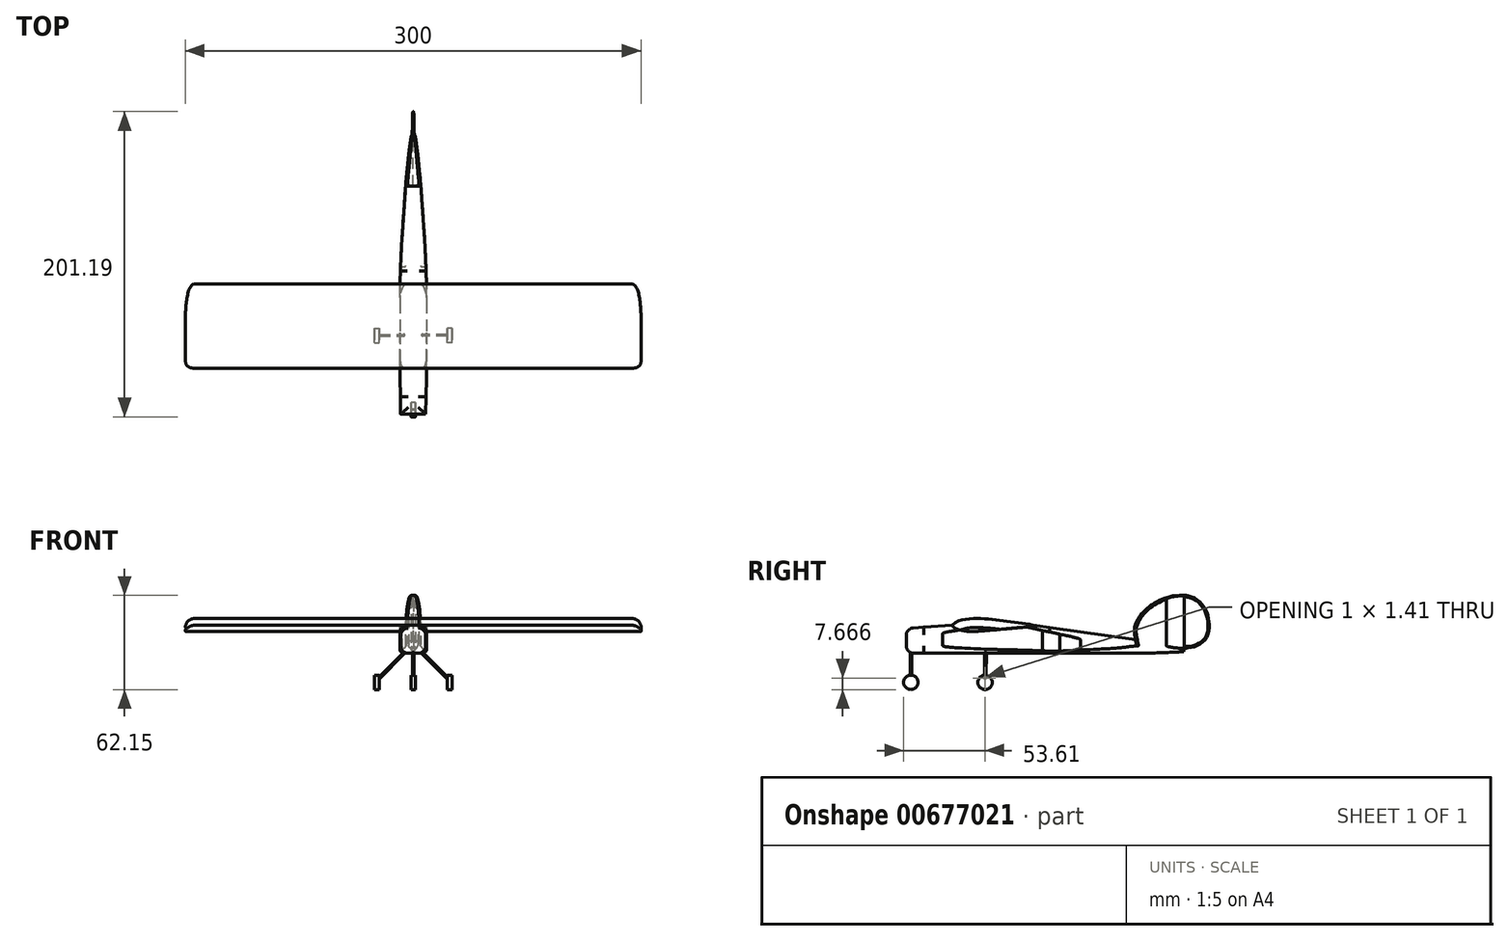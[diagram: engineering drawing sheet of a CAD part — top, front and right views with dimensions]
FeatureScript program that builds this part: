
annotation { "Feature Type Name" : "Feature", "Feature Type Description" : "" }
export const myFeature = defineFeature(function(context is Context, id is Id, definition is map)
    precondition{}
    {
        {
            var Q0;
            Q0=qCreatedBy(makeId("Top.planeOp"),FACE);
            var sketch = newSketch(context, id + "F0", { "sketchPlane" : qUnion([Q0])});
            skPoint(sketch, "E0", {"position": v(-29, 19.94) * mm});
            skLineSegment(sketch, "E1", {"start": v(0, 0) * mm, "end": v(8.25, 0) * mm});
            skLineSegment(sketch, "E2", {"start": v(8.25, 0) * mm, "end": v(8.4, 11.66) * mm});
            skLineSegment(sketch, "E3", {"start": v(8.4, 11.66) * mm, "end": v(8.64, 23.9) * mm});
            skLineSegment(sketch, "E4", {"start": v(8.64, 23.9) * mm, "end": v(8.64, 30.7) * mm});
            skLineSegment(sketch, "E5", {"start": v(8.64, 30.7) * mm, "end": v(8.64, 38.91) * mm});
            skLineSegment(sketch, "E6", {"start": v(8.64, 38.91) * mm, "end": v(8.64, 53.75) * mm});
            skLineSegment(sketch, "E7", {"start": v(8.64, 53.75) * mm, "end": v(8.71, 73.84) * mm});
            skLineSegment(sketch, "E8", {"start": v(8.71, 73.84) * mm, "end": v(8.71, 77.09) * mm});
            skLineSegment(sketch, "E9", {"start": v(8.71, 77.09) * mm, "end": v(8.61, 89.68) * mm});
            skLineSegment(sketch, "E10", {"start": v(8.61, 89.68) * mm, "end": v(8.2, 101.14) * mm});
            skLineSegment(sketch, "E11", {"start": v(8.2, 101.14) * mm, "end": v(7.51, 114.78) * mm});
            skLineSegment(sketch, "E12", {"start": v(7.51, 114.78) * mm, "end": v(5.18, 148.4) * mm});
            skLineSegment(sketch, "E13", {"start": v(5.18, 148.4) * mm, "end": v(3.01, 171.13) * mm});
            skLineSegment(sketch, "E14", {"start": v(3.01, 171.13) * mm, "end": v(1.43, 183.1) * mm});
            skLineSegment(sketch, "E15", {"start": v(1.43, 183.1) * mm, "end": v(0.72, 183.1) * mm});
            skLineSegment(sketch, "E16", {"start": v(0, 0) * mm, "end": v(0, 183.1) * mm});
            skLineSegment(sketch, "E17.MirrorCS", {"start": v(-5.18, 148.4) * mm, "end": v(-3.01, 171.13) * mm});
            skLineSegment(sketch, "E18.MirrorCS", {"start": v(-3.01, 171.13) * mm, "end": v(-1.43, 183.1) * mm});
            skLineSegment(sketch, "E19.MirrorCS", {"start": v(-1.43, 183.1) * mm, "end": v(-0.72, 183.1) * mm});
            skLineSegment(sketch, "E20.MirrorCS", {"start": v(-7.51, 114.78) * mm, "end": v(-5.18, 148.4) * mm});
            skLineSegment(sketch, "E21.MirrorCS", {"start": v(-8.61, 89.68) * mm, "end": v(-8.2, 101.14) * mm});
            skLineSegment(sketch, "E22.MirrorCS", {"start": v(-8.71, 77.09) * mm, "end": v(-8.61, 89.68) * mm});
            skLineSegment(sketch, "E23.MirrorCS", {"start": v(-8.2, 101.14) * mm, "end": v(-7.51, 114.78) * mm});
            skLineSegment(sketch, "E24.MirrorCS", {"start": v(-8.64, 53.75) * mm, "end": v(-8.71, 73.84) * mm});
            skLineSegment(sketch, "E25.MirrorCS", {"start": v(-8.64, 38.91) * mm, "end": v(-8.64, 53.75) * mm});
            skLineSegment(sketch, "E26.MirrorCS", {"start": v(-8.64, 23.9) * mm, "end": v(-8.64, 30.7) * mm});
            skLineSegment(sketch, "E27.MirrorCS", {"start": v(-8.64, 30.7) * mm, "end": v(-8.64, 38.91) * mm});
            skLineSegment(sketch, "E28.MirrorCS", {"start": v(-8.4, 11.66) * mm, "end": v(-8.64, 23.9) * mm});
            skLineSegment(sketch, "E29.MirrorCS", {"start": v(-8.25, 0) * mm, "end": v(-8.4, 11.66) * mm});
            skLineSegment(sketch, "E30", {"start": v(-0.72, 183.1) * mm, "end": v(-0.34, 199.72) * mm});
            skLineSegment(sketch, "E31", {"start": v(0.72, 183.1) * mm, "end": v(0.31, 199.7) * mm});
            skArc(sketch, "E32", {"start": v(0.31, 199.7) * mm, "mid": v(0, 200.02) * mm, "end": v(-0.34, 199.72) * mm});
            skLineSegment(sketch, "E33", {"start": v(-8.25, 0) * mm, "end": v(0, 0) * mm});
            skLineSegment(sketch, "E34", {"start": v(-8.71, 73.84) * mm, "end": v(-8.71, 77.09) * mm});
            skSolve(sketch);
        }
        {
            var Q0;
            Q0=qCreatedBy(makeId("Right.planeOp"),FACE);
            var sketch = newSketch(context, id + "F1", { "sketchPlane" : qUnion([Q0])});
            skPoint(sketch, "E35", {"position": v(9.53, 28.77) * mm});
            skLineSegment(sketch, "E36", {"start": v(9.53, 28.77) * mm, "end": v(9.53, 58.18) * mm});
            skLineSegment(sketch, "E37", {"start": v(0, 6.73) * mm, "end": v(0, 7.52) * mm});
            skLineSegment(sketch, "E38", {"start": v(0, 7.52) * mm, "end": v(30.35, 9.6) * mm});
            skFitSpline(sketch, "E39", {"points": [v(30.35, 9.6) * mm, v(30.74, 8.85) * mm, v(32.06, 7.7) * mm, v(33.67, 6.97) * mm, v(36.02, 6.27) * mm, v(40.27, 5.57) * mm, v(46.3, 5.57) * mm, v(51.85, 6) * mm, v(61.06, 6.76) * mm, v(70.26, 7.62) * mm, v(83.75, 8.9) * mm, v(85.82, 9.15) * mm], "startDerivative": vector(7.09, -18.14) * mm, "endDerivative": vector(24.4, 3.5) * mm});
            skLineSegment(sketch, "E40", {"start": v(85.82, 9.15) * mm, "end": v(94.4, 8) * mm});
            skLineSegment(sketch, "E41", {"start": v(94.4, 8) * mm, "end": v(130.2, 2.9) * mm});
            skLineSegment(sketch, "E42", {"start": v(130.2, 2.9) * mm, "end": v(150.98, -0.06) * mm});
            skLineSegment(sketch, "E43", {"start": v(150.98, -0.06) * mm, "end": v(150.98, -0.8) * mm});
            skLineSegment(sketch, "E44", {"start": v(150.98, -0.8) * mm, "end": v(182.74, -5.52) * mm});
            skLineSegment(sketch, "E45", {"start": v(182.74, -5.52) * mm, "end": v(182.74, -8.83) * mm});
            skLineSegment(sketch, "E46", {"start": v(182.74, -8.83) * mm, "end": v(97.77, -8.9) * mm});
            skLineSegment(sketch, "E47", {"start": v(97.77, -8.9) * mm, "end": v(15.77, -8.9) * mm});
            skLineSegment(sketch, "E48", {"start": v(15.77, -8.9) * mm, "end": v(0, -8.9) * mm});
            skLineSegment(sketch, "E49", {"start": v(0, -8.9) * mm, "end": v(0, 0) * mm});
            skFitSpline(sketch, "E50", {"points": [v(30.35, 9.6) * mm, v(31.65, 10.88) * mm, v(34.45, 12.35) * mm, v(39.4, 13.6) * mm, v(44.05, 13.96) * mm, v(51.46, 13.89) * mm, v(60.53, 13.02) * mm, v(70.8, 11.66) * mm, v(80.77, 10.16) * mm, v(85.82, 9.15) * mm], "startDerivative": vector(18.65, 21.26) * mm, "endDerivative": vector(44.49, -9.56) * mm});
            skFitSpline(sketch, "E51", {"points": [v(150.98, -0.06) * mm, v(150.73, 1.38) * mm, v(150.26, 4.22) * mm, v(150.22, 7.02) * mm, v(151.56, 11.72) * mm, v(154.77, 16.71) * mm, v(161.1, 22.75) * mm, v(167.85, 26.44) * mm, v(173.09, 28.4) * mm, v(178.35, 29.11) * mm, v(183.08, 29.3) * mm, v(188.07, 28.35) * mm, v(192.81, 25.62) * mm, v(197.13, 20.08) * mm, v(198.92, 15.11) * mm, v(199.6, 10.29) * mm, v(199.64, 7.48) * mm, v(199.22, 4.9) * mm, v(197.73, 0.97) * mm, v(194.97, -1.94) * mm, v(190.97, -4.24) * mm, v(186.66, -5.33) * mm, v(182.74, -5.52) * mm], "startDerivative": vector(-8.61, 50.6) * mm, "endDerivative": vector(-92.07, -0.95) * mm});
            skLineSegment(sketch, "E52", {"start": v(0, 6.73) * mm, "end": v(0, 0) * mm});
            skSolve(sketch);
        }
        {
            var Q0;
            Q0 = qSketchRegion(id + "F1", true);
            extrude(context, id + "F2", {"entities" : qUnion([Q0]), "endBound" : BoundingType.SYMMETRIC, "depth" : 100 * mm, "offsetDistance" : 25 * mm});
        }
        {
            var Q0;
            Q0 = qSketchRegion(id + "F0", true);
            extrude(context, id + "F3", {"entities" : qUnion([Q0]), "endBound" : BoundingType.SYMMETRIC, "depth" : 100 * mm, "offsetDistance" : 25 * mm});
        }
        {
            var Q0;
            Q0=makeQuery(id+"F2.opExtrude","SWEPT_BODY",BODY,{"disambiguationData":[OSD([sQuery(id+"F1.wireOp",EDGE,"E37"),sQuery(id+"F1.wireOp",EDGE,"E38"),sQuery(id+"F1.wireOp",EDGE,"E40"),sQuery(id+"F1.wireOp",EDGE,"E41"),sQuery(id+"F1.wireOp",EDGE,"E42"),sQuery(id+"F1.wireOp",EDGE,"E45"),sQuery(id+"F1.wireOp",EDGE,"E46"),sQuery(id+"F1.wireOp",EDGE,"E47"),sQuery(id+"F1.wireOp",EDGE,"E48"),sQuery(id+"F1.wireOp",EDGE,"E49"),sQuery(id+"F1.wireOp",EDGE,"E50"),sQuery(id+"F1.wireOp",EDGE,"E51"),sQuery(id+"F1.wireOp",EDGE,"E52")])]});
            var Q1;
            Q1=makeQuery(id+"F3.opExtrude","SWEPT_BODY",BODY,{"disambiguationData":[OSD([sQuery(id+"F0.wireOp",EDGE,"E1"),sQuery(id+"F0.wireOp",EDGE,"E2"),sQuery(id+"F0.wireOp",EDGE,"E3"),sQuery(id+"F0.wireOp",EDGE,"E4"),sQuery(id+"F0.wireOp",EDGE,"E5"),sQuery(id+"F0.wireOp",EDGE,"E6"),sQuery(id+"F0.wireOp",EDGE,"E7"),sQuery(id+"F0.wireOp",EDGE,"E8"),sQuery(id+"F0.wireOp",EDGE,"E9"),sQuery(id+"F0.wireOp",EDGE,"E10"),sQuery(id+"F0.wireOp",EDGE,"E11"),sQuery(id+"F0.wireOp",EDGE,"E12"),sQuery(id+"F0.wireOp",EDGE,"E13"),sQuery(id+"F0.wireOp",EDGE,"E14"),sQuery(id+"F0.wireOp",EDGE,"E15"),sQuery(id+"F0.wireOp",EDGE,"E17.MirrorCS"),sQuery(id+"F0.wireOp",EDGE,"E18.MirrorCS"),sQuery(id+"F0.wireOp",EDGE,"E19.MirrorCS"),sQuery(id+"F0.wireOp",EDGE,"E20.MirrorCS"),sQuery(id+"F0.wireOp",EDGE,"E21.MirrorCS"),sQuery(id+"F0.wireOp",EDGE,"E22.MirrorCS"),sQuery(id+"F0.wireOp",EDGE,"E23.MirrorCS"),sQuery(id+"F0.wireOp",EDGE,"E24.MirrorCS"),sQuery(id+"F0.wireOp",EDGE,"E26.MirrorCS"),sQuery(id+"F0.wireOp",EDGE,"E28.MirrorCS"),sQuery(id+"F0.wireOp",EDGE,"E25.MirrorCS"),sQuery(id+"F0.wireOp",EDGE,"E27.MirrorCS"),sQuery(id+"F0.wireOp",EDGE,"E29.MirrorCS"),sQuery(id+"F0.wireOp",EDGE,"E30"),sQuery(id+"F0.wireOp",EDGE,"E31"),sQuery(id+"F0.wireOp",EDGE,"E32"),sQuery(id+"F0.wireOp",EDGE,"E33"),sQuery(id+"F0.wireOp",EDGE,"E34")])]});
            booleanBodies(context, id + "F4", {"operationType" : BooleanOperationType.INTERSECTION, "tools" : qUnion([Q0, Q1])});
        }
        {
            var Q0;
            Q0=makeQuery(id+"F1.imprint","IMPRINT",FACE,{"disambiguationData":[TD([[makeQuery(id+"F1.imprint","IMPRINT",EDGE,{"derivedFrom":sQuery(id+"F1.wireOp",EDGE,"E39")}),1.0]])]});
            extrude(context, id + "F5", {"entities" : qUnion([Q0]), "operationType" : NewBodyOperationType.ADD, "endBound" : BoundingType.SYMMETRIC, "depth" : 300 * mm, "offsetDistance" : 25 * mm});
        }
        {
            var Q0;
            Q0=makeQuery(id+"F2.opExtrude","SWEPT_FACE",FACE,{"disambiguationData":[OSD([sQuery(id+"F1.wireOp",EDGE,"E47"),sQuery(id+"F1.wireOp",EDGE,"E48")])]});
            var sketch = newSketch(context, id + "F6", { "sketchPlane" : qUnion([Q0])});
            skCircle(sketch, "E53", {"center": v(0, -3.04) * mm, "radius": 0.5 * mm});
            skSolve(sketch);
        }
        {
            var Q0;
            Q0 = qSketchRegion(id + "F6", true);
            extrude(context, id + "F7", {"entities" : qUnion([Q0]), "operationType" : NewBodyOperationType.ADD, "depth" : 18.9 * mm, "offsetDistance" : 25 * mm});
        }
        {
            var Q0;
            Q0=qCreatedBy(makeId("Right.planeOp"),FACE);
            var sketch = newSketch(context, id + "F8", { "sketchPlane" : qUnion([Q0])});
            skCircle(sketch, "E54", {"center": v(3, -28.04) * mm, "radius": 4.75 * mm});
            skPoint(sketch, "E54.first.point", {"position": v(5.3, -23.89) * mm});
            skPoint(sketch, "E54.second.point", {"position": v(0.42, -32.02) * mm});
            skPoint(sketch, "E54.third.point", {"position": v(7.11, -30.4) * mm});
            skSolve(sketch);
        }
        {
            var Q0;
            Q0 = qSketchRegion(id + "F8", true);
            extrude(context, id + "F9", {"entities" : qUnion([Q0]), "operationType" : NewBodyOperationType.ADD, "endBound" : BoundingType.SYMMETRIC, "depth" : 3 * mm, "offsetDistance" : 25 * mm});
        }
        {
            var Q0;
            Q0=makeQuery(id+"F4.opBoolean","INTERSECT",EDGE,{"derivedFrom":[makeQuery(id+"F2.opExtrude","SWEPT_FACE",FACE,{"disambiguationData":[OSD([sQuery(id+"F1.wireOp",EDGE,"E38")])]}),makeQuery(id+"F3.opExtrude","SWEPT_FACE",FACE,{"disambiguationData":[OSD([sQuery(id+"F0.wireOp",EDGE,"E2")])]})]});
            var Q1;
            Q1=makeQuery(id+"F2.opExtrude","SWEPT_EDGE",EDGE,{"disambiguationData":[OSD([sQuery(id+"F1.wireOp",EDGE,"E37"),sQuery(id+"F1.wireOp",EDGE,"E38")])]});
            var Q2;
            Q2=makeQuery(id+"F4.opBoolean","INTERSECT",EDGE,{"derivedFrom":[makeQuery(id+"F2.opExtrude","SWEPT_FACE",FACE,{"disambiguationData":[OSD([sQuery(id+"F1.wireOp",EDGE,"E38")])]}),makeQuery(id+"F3.opExtrude","SWEPT_FACE",FACE,{"disambiguationData":[OSD([sQuery(id+"F0.wireOp",EDGE,"E29.MirrorCS")])]})]});
            var Q3;
            Q3=makeQuery(id+"F3.opExtrude","SWEPT_EDGE",EDGE,{"disambiguationData":[OSD([sQuery(id+"F0.wireOp",EDGE,"E29.MirrorCS"),sQuery(id+"F0.wireOp",EDGE,"E33")])]});
            var Q4;
            Q4=makeQuery(id+"F3.opExtrude","SWEPT_EDGE",EDGE,{"disambiguationData":[OSD([sQuery(id+"F0.wireOp",EDGE,"E1"),sQuery(id+"F0.wireOp",EDGE,"E2")])]});
            var Q5;
            Q5=makeQuery(id+"F2.opExtrude","SWEPT_EDGE",EDGE,{"disambiguationData":[OSD([sQuery(id+"F1.wireOp",EDGE,"E48"),sQuery(id+"F1.wireOp",EDGE,"E49")])]});
            var Q6;
            Q6=makeQuery(id+"F4.opBoolean","INTERSECT",EDGE,{"derivedFrom":[makeQuery(id+"F2.opExtrude","SWEPT_FACE",FACE,{"disambiguationData":[OSD([sQuery(id+"F1.wireOp",EDGE,"E47"),sQuery(id+"F1.wireOp",EDGE,"E48")])]}),makeQuery(id+"F3.opExtrude","SWEPT_FACE",FACE,{"disambiguationData":[OSD([sQuery(id+"F0.wireOp",EDGE,"E2")])]})]});
            var Q7;
            Q7=makeQuery(id+"F4.opBoolean","INTERSECT",EDGE,{"derivedFrom":[makeQuery(id+"F2.opExtrude","SWEPT_FACE",FACE,{"disambiguationData":[OSD([sQuery(id+"F1.wireOp",EDGE,"E47"),sQuery(id+"F1.wireOp",EDGE,"E48")])]}),makeQuery(id+"F3.opExtrude","SWEPT_FACE",FACE,{"disambiguationData":[OSD([sQuery(id+"F0.wireOp",EDGE,"E29.MirrorCS")])]})]});
            var Q8;
            Q8=makeQuery(id+"F4.opBoolean","INTERSECT",EDGE,{"derivedFrom":[makeQuery(id+"F2.opExtrude","SWEPT_FACE",FACE,{"disambiguationData":[OSD([sQuery(id+"F1.wireOp",EDGE,"E41"),sQuery(id+"F1.wireOp",EDGE,"E42")])]}),makeQuery(id+"F3.opExtrude","SWEPT_FACE",FACE,{"disambiguationData":[OSD([sQuery(id+"F0.wireOp",EDGE,"E12")])]})]});
            var Q9;
            Q9=makeQuery(id+"F4.opBoolean","INTERSECT",EDGE,{"derivedFrom":[makeQuery(id+"F2.opExtrude","SWEPT_FACE",FACE,{"disambiguationData":[OSD([sQuery(id+"F1.wireOp",EDGE,"E41"),sQuery(id+"F1.wireOp",EDGE,"E42")])]}),makeQuery(id+"F3.opExtrude","SWEPT_FACE",FACE,{"disambiguationData":[OSD([sQuery(id+"F0.wireOp",EDGE,"E20.MirrorCS")])]})]});
            fillet(context, id + "F10", {"entities" : qUnion([Q0, Q1, Q2, Q3, Q4, Q5, Q6, Q7, Q8, Q9]), "radius" : 5 * mm, "tangentPropagation" : true, "allowEdgeOverflow" : false});
        }
        {
            var Q0;
            Q0=makeQuery(id+"F4.opBoolean","INTERSECT",EDGE,{"derivedFrom":[makeQuery(id+"F2.opExtrude","SWEPT_FACE",FACE,{"disambiguationData":[OSD([sQuery(id+"F1.wireOp",EDGE,"E46")])]}),makeQuery(id+"F3.opExtrude","SWEPT_FACE",FACE,{"disambiguationData":[OSD([sQuery(id+"F0.wireOp",EDGE,"E13")])]})]});
            var Q1;
            Q1=makeQuery(id+"F4.opBoolean","INTERSECT",EDGE,{"derivedFrom":[makeQuery(id+"F2.opExtrude","SWEPT_FACE",FACE,{"disambiguationData":[OSD([sQuery(id+"F1.wireOp",EDGE,"E46")])]}),makeQuery(id+"F3.opExtrude","SWEPT_FACE",FACE,{"disambiguationData":[OSD([sQuery(id+"F0.wireOp",EDGE,"E17.MirrorCS")])]})]});
            fillet(context, id + "F11", {"entities" : qUnion([Q0, Q1]), "radius" : 5 * mm, "tangentPropagation" : true, "allowEdgeOverflow" : false});
        }
        {
            var Q0;
            Q0=makeQuery(id+"F4.opBoolean","INTERSECT",EDGE,{"derivedFrom":[makeQuery(id+"F2.opExtrude","SWEPT_FACE",FACE,{"disambiguationData":[OSD([sQuery(id+"F1.wireOp",EDGE,"E51")])]}),makeQuery(id+"F3.opExtrude","SWEPT_FACE",FACE,{"disambiguationData":[OSD([sQuery(id+"F0.wireOp",EDGE,"E13")])]})]});
            var Q1;
            Q1=makeQuery(id+"F4.opBoolean","INTERSECT",EDGE,{"derivedFrom":[makeQuery(id+"F2.opExtrude","SWEPT_FACE",FACE,{"disambiguationData":[OSD([sQuery(id+"F1.wireOp",EDGE,"E51")])]}),makeQuery(id+"F3.opExtrude","SWEPT_FACE",FACE,{"disambiguationData":[OSD([sQuery(id+"F0.wireOp",EDGE,"E17.MirrorCS")])]})]});
            fillet(context, id + "F12", {"entities" : qUnion([Q0, Q1]), "radius" : 1 * mm, "tangentPropagation" : true, "allowEdgeOverflow" : false});
        }
        {
            var Q0;
            Q0=makeQuery(id+"F3.opExtrude","SWEPT_EDGE",EDGE,{"disambiguationData":[OSD([sQuery(id+"F0.wireOp",EDGE,"E15"),sQuery(id+"F0.wireOp",EDGE,"E31")])]});
            var Q1;
            Q1=makeQuery(id+"F3.opExtrude","SWEPT_EDGE",EDGE,{"disambiguationData":[OSD([sQuery(id+"F0.wireOp",EDGE,"E19.MirrorCS"),sQuery(id+"F0.wireOp",EDGE,"E30")])]});
            fillet(context, id + "F13", {"entities" : qUnion([Q0, Q1]), "radius" : 4 * mm, "tangentPropagation" : true, "allowEdgeOverflow" : false});
        }
        {
            var Q0;
            Q0=makeQuery(id+"F4.opBoolean","INTERSECT",EDGE,{"derivedFrom":[makeQuery(id+"F2.opExtrude","SWEPT_FACE",FACE,{"disambiguationData":[OSD([sQuery(id+"F1.wireOp",EDGE,"E51")])]}),makeQuery(id+"F3.opExtrude","SWEPT_FACE",FACE,{"disambiguationData":[OSD([sQuery(id+"F0.wireOp",EDGE,"E31")])]})]});
            var Q1;
            Q1=makeQuery(id+"F4.opBoolean","INTERSECT",EDGE,{"derivedFrom":[makeQuery(id+"F2.opExtrude","SWEPT_FACE",FACE,{"disambiguationData":[OSD([sQuery(id+"F1.wireOp",EDGE,"E51")])]}),makeQuery(id+"F3.opExtrude","SWEPT_FACE",FACE,{"disambiguationData":[OSD([sQuery(id+"F0.wireOp",EDGE,"E30")])]})]});
            fillet(context, id + "F14", {"entities" : qUnion([Q0, Q1]), "radius" : 1 * mm, "tangentPropagation" : true, "allowEdgeOverflow" : false});
        }
        {
            var Q0;
            Q0=makeQuery(id+"F5.opExtrude","CAP_EDGE",EDGE,{"disambiguationData":[OSD([sQuery(id+"F1.wireOp",EDGE,"E50")])],"isStart":false});
            var Q1;
            Q1=makeQuery(id+"F5.opExtrude","CAP_EDGE",EDGE,{"disambiguationData":[OSD([sQuery(id+"F1.wireOp",EDGE,"E50")])],"isStart":true});
            fillet(context, id + "F15", {"entities" : qUnion([Q0, Q1]), "radius" : 6 * mm, "tangentPropagation" : true, "allowEdgeOverflow" : false});
        }
        {
            var Q0;
            Q0=makeQuery(id+"F2.opExtrude","SWEPT_FACE",FACE,{"disambiguationData":[OSD([sQuery(id+"F1.wireOp",EDGE,"E47"),sQuery(id+"F1.wireOp",EDGE,"E48")])]});
            var sketch = newSketch(context, id + "F16", { "sketchPlane" : qUnion([Q0])});
            skCircle(sketch, "E55", {"center": v(3.52, -52.19) * mm, "radius": 0.5 * mm});
            skSolve(sketch);
        }
        {
            var Q0;
            Q0 = qSketchRegion(id + "F16", true);
            extrude(context, id + "F17", {"entities" : qUnion([Q0]), "depth" : 25 * mm, "offsetDistance" : 25 * mm});
        }
        {
            var Q0;
            Q0=makeQuery(id+"F17.opExtrude","SWEPT_BODY",BODY,{"disambiguationData":[OSD([sQuery(id+"F16.wireOp",EDGE,"E55")])]});
            var Q1;
            {var subQ0=makeQuery(id+"F2.opExtrude","SWEPT_FACE",FACE,{"disambiguationData":[OSD([sQuery(id+"F1.wireOp",EDGE,"E47"),sQuery(id+"F1.wireOp",EDGE,"E48")])]});Q1=makeQuery(id+"F10.opFillet","BLEND_EDGE",EDGE,{"blendedFrom":[makeQuery(id+"F4.opBoolean","INTERSECT",EDGE,{"derivedFrom":[subQ0,makeQuery(id+"F3.opExtrude","SWEPT_FACE",FACE,{"disambiguationData":[OSD([sQuery(id+"F0.wireOp",EDGE,"E3")])]})]}),subQ0],"blendedInto":[subQ0]});}
            transform(context, id + "F18", {"entities" : qUnion([Q0]), "transformType" : TransformType.ROTATION, "transformAxis" : qUnion([Q1]), "angle" : 45 * degree, "oppositeDirection" : true, "makeCopy" : false});
        }
        {
            var Q0;
            Q0=makeQuery(id+"F17.opExtrude","SWEPT_BODY",BODY,{"disambiguationData":[OSD([sQuery(id+"F16.wireOp",EDGE,"E55")])]});
            transform(context, id + "F19", {"entities" : qUnion([Q0]), "transformType" : TransformType.TRANSLATION_3D, "dx" : 2 * mm, "dy" : 0 * mm, "dz" : 1 * mm, "makeCopy" : false});
        }
        {
            var Q0;
            Q0=makeQuery(id+"F17.opExtrude","SWEPT_BODY",BODY,{"disambiguationData":[OSD([sQuery(id+"F16.wireOp",EDGE,"E55")])]});
            var Q1;
            Q1=qCreatedBy(makeId("Right.planeOp"),FACE);
            mirror(context, id + "F20", {"operationType" : NewBodyOperationType.ADD, "entities" : qUnion([Q0]), "mirrorPlane" : qUnion([Q1])});
        }
        {
            var Q0;
            Q0=qCreatedBy(makeId("Right.planeOp"),FACE);
            cPlane(context, id + "F21", {"entities" : qUnion([Q0]), "cplaneType" : CPlaneType.OFFSET, "offset" : 24 * mm, "width" : 150 * mm, "height" : 150 * mm});
        }
        {
            var Q0;
            Q0=qCreatedBy(id+"F21.planeOp",FACE);
            var sketch = newSketch(context, id + "F22", { "sketchPlane" : qUnion([Q0])});
            skCircle(sketch, "E56", {"center": v(51.88, -28.07) * mm, "radius": 4.75 * mm});
            skSolve(sketch);
        }
        {
            var Q0;
            Q0 = qSketchRegion(id + "F22", true);
            extrude(context, id + "F23", {"entities" : qUnion([Q0]), "endBound" : BoundingType.SYMMETRIC, "depth" : 3 * mm, "offsetDistance" : 25 * mm});
        }
        {
            var Q0;
            Q0=makeQuery(id+"F23.opExtrude","SWEPT_BODY",BODY,{"disambiguationData":[OSD([sQuery(id+"F22.wireOp",EDGE,"E56")])]});
            var Q1;
            Q1=qCreatedBy(makeId("Right.planeOp"),FACE);
            mirror(context, id + "F24", {"operationType" : NewBodyOperationType.ADD, "entities" : qUnion([Q0]), "mirrorPlane" : qUnion([Q1])});
        }
    });
